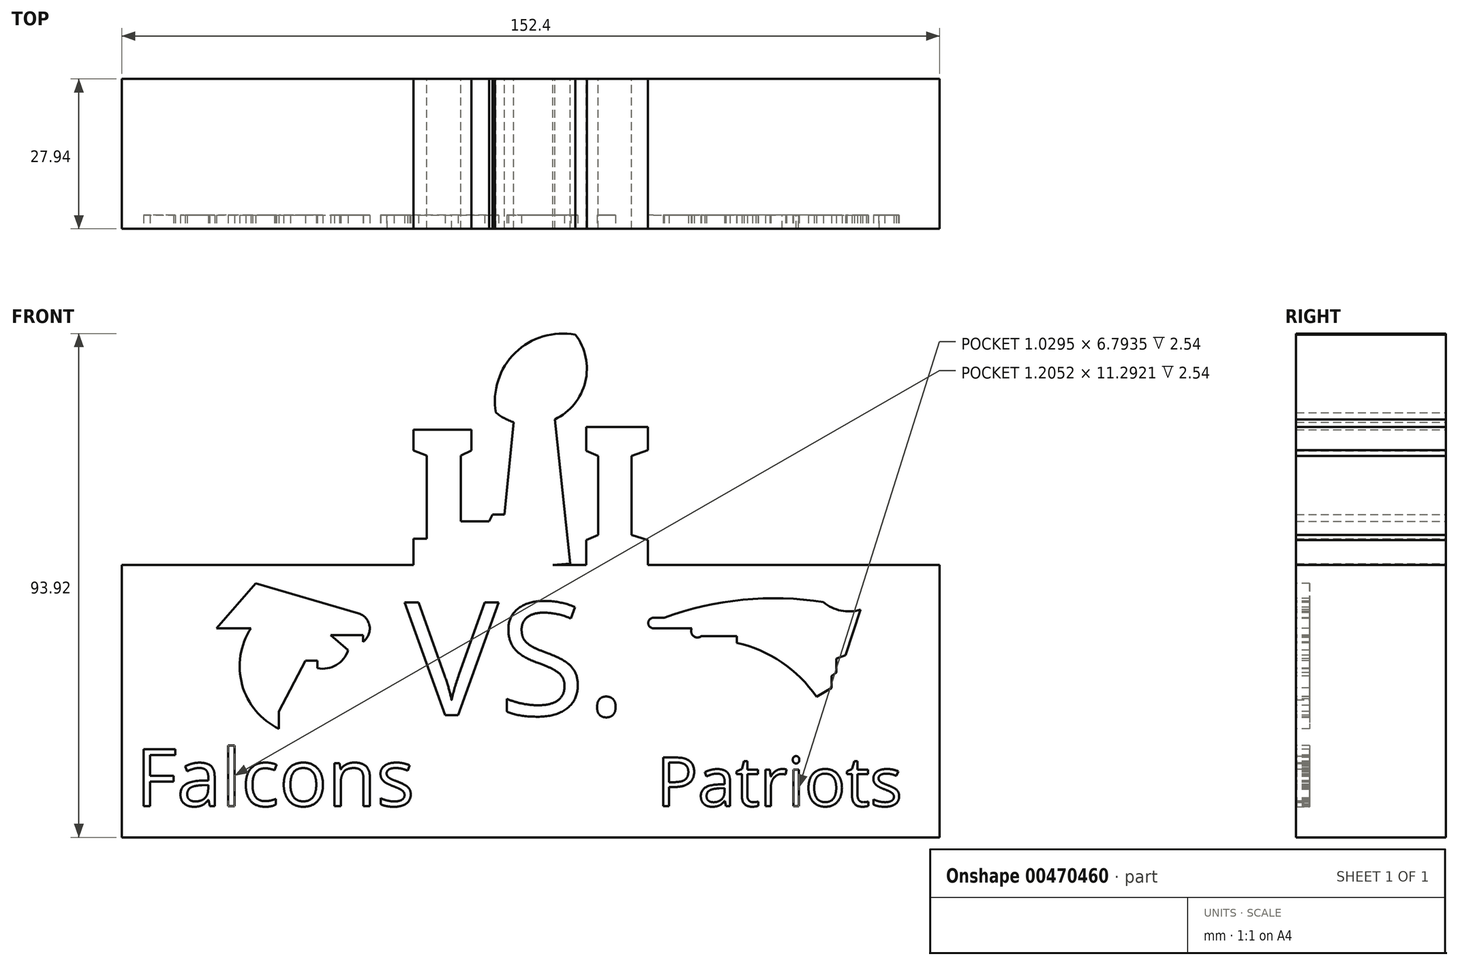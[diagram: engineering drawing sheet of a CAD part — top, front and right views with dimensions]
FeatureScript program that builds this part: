
annotation { "Feature Type Name" : "Feature", "Feature Type Description" : "" }
export const myFeature = defineFeature(function(context is Context, id is Id, definition is map)
    precondition{}
    {
        {
            var Q0;
            Q0=qCreatedBy(makeId("Front.planeOp"),FACE);
            var sketch = newSketch(context, id + "F0", { "sketchPlane" : qUnion([Q0])});
            skLineSegment(sketch, "E0.bottom", {"start": v(-75.1, 6.56) * mm, "end": v(77.3, 6.56) * mm});
            skLineSegment(sketch, "E0.top", {"start": v(-75.1, -44.24) * mm, "end": v(77.3, -44.24) * mm});
            skLineSegment(sketch, "E0.left", {"start": v(-75.1, 6.56) * mm, "end": v(-75.1, -44.24) * mm});
            skLineSegment(sketch, "E0.right", {"start": v(77.3, 6.56) * mm, "end": v(77.3, -44.24) * mm});
            skLineSegment(sketch, "E1", {"start": v(-20.74, 31.75) * mm, "end": v(-20.74, 27.9) * mm});
            skLineSegment(sketch, "E2", {"start": v(-20.74, 27.9) * mm, "end": v(-18.26, 26.95) * mm});
            skLineSegment(sketch, "E3", {"start": v(-18.26, 26.95) * mm, "end": v(-18.26, 11.44) * mm});
            skLineSegment(sketch, "E4", {"start": v(-18.26, 11.44) * mm, "end": v(-20.74, 11.44) * mm});
            skLineSegment(sketch, "E5", {"start": v(-20.74, 11.44) * mm, "end": v(-20.74, 6.56) * mm});
            skLineSegment(sketch, "E6", {"start": v(-20.74, 6.56) * mm, "end": v(5.21, 6.56) * mm});
            skLineSegment(sketch, "E7", {"start": v(3.63, 32.96) * mm, "end": v(5.21, 6.56) * mm});
            skLineSegment(sketch, "E8", {"start": v(5.21, 6.56) * mm, "end": v(8.44, 6.76) * mm});
            skLineSegment(sketch, "E9", {"start": v(8.44, 6.76) * mm, "end": v(5.6, 33.67) * mm});
            skLineSegment(sketch, "E10", {"start": v(-2.05, 33.14) * mm, "end": v(-3.76, 15.92) * mm});
            skLineSegment(sketch, "E11", {"start": v(-20.74, 31.75) * mm, "end": v(-9.95, 31.75) * mm});
            skLineSegment(sketch, "E12", {"start": v(-9.95, 31.75) * mm, "end": v(-9.95, 27.9) * mm});
            skLineSegment(sketch, "E13", {"start": v(-9.95, 27.9) * mm, "end": v(-11.92, 26.95) * mm});
            skLineSegment(sketch, "E14", {"start": v(-11.92, 26.95) * mm, "end": v(-11.92, 14.64) * mm});
            skLineSegment(sketch, "E15", {"start": v(-11.92, 14.64) * mm, "end": v(-6.63, 14.64) * mm});
            skLineSegment(sketch, "E16", {"start": v(-6.63, 14.64) * mm, "end": v(-6.03, 15.92) * mm});
            skLineSegment(sketch, "E17", {"start": v(-6.03, 15.92) * mm, "end": v(-3.76, 15.92) * mm});
            skLineSegment(sketch, "E18", {"start": v(-3.76, 15.92) * mm, "end": v(-3.76, 6.76) * mm});
            skArc(sketch, "E19", {"start": v(9.43, 49.45) * mm, "mid": v(-1.8, 46.07) * mm, "end": v(-5.4, 34.92) * mm});
            skArc(sketch, "E20", {"start": v(-5.4, 34.92) * mm, "mid": v(8.42, 35.64) * mm, "end": v(9.43, 49.45) * mm});
            skLineSegment(sketch, "E21", {"start": v(11.43, 27.82) * mm, "end": v(13.68, 26.87) * mm});
            skLineSegment(sketch, "E22", {"start": v(13.68, 26.87) * mm, "end": v(13.68, 12.13) * mm});
            skLineSegment(sketch, "E23", {"start": v(13.68, 12.13) * mm, "end": v(11.43, 11.19) * mm});
            skLineSegment(sketch, "E24", {"start": v(11.43, 11.19) * mm, "end": v(11.43, 6.56) * mm});
            skLineSegment(sketch, "E25", {"start": v(11.43, 6.56) * mm, "end": v(22.95, 6.56) * mm});
            skLineSegment(sketch, "E26", {"start": v(22.95, 6.56) * mm, "end": v(22.95, 11.19) * mm});
            skLineSegment(sketch, "E27", {"start": v(22.95, 11.19) * mm, "end": v(19.87, 12.13) * mm});
            skLineSegment(sketch, "E28", {"start": v(19.87, 12.13) * mm, "end": v(19.87, 26.87) * mm});
            skLineSegment(sketch, "E29", {"start": v(19.87, 26.87) * mm, "end": v(22.95, 27.95) * mm});
            skLineSegment(sketch, "E30", {"start": v(22.95, 27.95) * mm, "end": v(22.95, 32.23) * mm});
            skLineSegment(sketch, "E31", {"start": v(22.95, 32.23) * mm, "end": v(11.43, 32.23) * mm});
            skLineSegment(sketch, "E32", {"start": v(11.43, 32.23) * mm, "end": v(11.43, 27.82) * mm});
            skSolve(sketch);
        }
        {
            var Q0;
            Q0 = qSketchRegion(id + "F0", true);
            extrude(context, id + "F1", {"entities" : qUnion([Q0]), "depth" : 27.94 * mm});
        }
        {
            var Q0;
            Q0=makeQuery(id+"F1.opExtrude","CAP_FACE",FACE,{"disambiguationData":[OSD([sQuery(id+"F0.wireOp",EDGE,"E0.bottom"),sQuery(id+"F0.wireOp",EDGE,"E0.top"),sQuery(id+"F0.wireOp",EDGE,"E0.left"),sQuery(id+"F0.wireOp",EDGE,"E0.right"),sQuery(id+"F0.wireOp",EDGE,"51d3c1c2-4678-4070-a935-1c2ae8ceac52"),sQuery(id+"F0.wireOp",EDGE,"f5bbca2f-ece1-45e4-84c9-4250c47298a3"),sQuery(id+"F0.wireOp",EDGE,"df2c12da-2ae3-4d1a-bf00-16d2e73c16a6"),sQuery(id+"F0.wireOp",EDGE,"ab1d8fd3-a22a-4d10-bc1b-4df98c300e8c"),sQuery(id+"F0.wireOp",EDGE,"32629ec4-7446-44ef-b423-ef05bb4e758c"),sQuery(id+"F0.wireOp",EDGE,"b3cf064b-aa9a-4bf5-8094-2338da96f838"),sQuery(id+"F0.wireOp",EDGE,"5fee9cea-6940-4a30-ae6c-49024f08f099"),sQuery(id+"F0.wireOp",EDGE,"3d6fc4a5-3aed-420e-b1e3-99403f750af0"),sQuery(id+"F0.wireOp",EDGE,"caa3e821-e804-49dc-9bb2-aabf213cfac6"),sQuery(id+"F0.wireOp",EDGE,"841424ae-1137-4768-b8eb-4dc3a59ec455"),sQuery(id+"F0.wireOp",EDGE,"84873b07-a760-4daf-8af0-85f94e43fe12"),sQuery(id+"F0.wireOp",EDGE,"49e816f2-52c8-406e-a4e7-44763c2afad2"),sQuery(id+"F0.wireOp",EDGE,"f34c5290-1b6a-42fb-a69f-c831adc31d09"),sQuery(id+"F0.wireOp",EDGE,"a4cf80c3-0732-48e7-8c47-b4bcee52f594"),sQuery(id+"F0.wireOp",EDGE,"aa5594db-ee71-498d-9179-3ce95b60c7d9"),sQuery(id+"F0.wireOp",EDGE,"7350933a-e141-4493-ad32-cfc7d2644b59"),sQuery(id+"F0.wireOp",EDGE,"028e278e-2f42-4de1-bc6f-db93ac8ad055"),sQuery(id+"F0.wireOp",EDGE,"cfd26f7e-d5b0-4229-bcee-958b32301bc1"),sQuery(id+"F0.wireOp",EDGE,"caddbf1c-78cf-4739-9aeb-5831cae17361"),sQuery(id+"F0.wireOp",EDGE,"15cb3bb8-4a25-48d3-b514-d85eaaf90072"),sQuery(id+"F0.wireOp",EDGE,"1946ed44-b253-4600-8266-74096e4aaf0f"),sQuery(id+"F0.wireOp",EDGE,"8db78c25-9355-4392-b348-b02de26508c2"),sQuery(id+"F0.wireOp",EDGE,"97191c49-12d8-4a6f-9165-80d11d1dd639"),sQuery(id+"F0.wireOp",EDGE,"61e6cfa5-2e70-4e35-bf5d-c662ff1ec202"),sQuery(id+"F0.wireOp",EDGE,"a59ac232-1a09-4b81-823e-92916a3a9cf0"),sQuery(id+"F0.wireOp",EDGE,"431d7071-b944-4f6a-b879-15e466296cc0"),sQuery(id+"F0.wireOp",EDGE,"83490649-d1fb-4782-b3b2-dd4396876af3"),sQuery(id+"F0.wireOp",EDGE,"fea7df3c-3f4f-4230-b99d-b53fc99c95d4"),sQuery(id+"F0.wireOp",EDGE,"E1"),sQuery(id+"F0.wireOp",EDGE,"E2"),sQuery(id+"F0.wireOp",EDGE,"E3"),sQuery(id+"F0.wireOp",EDGE,"E4"),sQuery(id+"F0.wireOp",EDGE,"E5"),sQuery(id+"F0.wireOp",EDGE,"E8"),sQuery(id+"F0.wireOp",EDGE,"E9"),sQuery(id+"F0.wireOp",EDGE,"E10"),sQuery(id+"F0.wireOp",EDGE,"E11"),sQuery(id+"F0.wireOp",EDGE,"E12"),sQuery(id+"F0.wireOp",EDGE,"E13"),sQuery(id+"F0.wireOp",EDGE,"E14"),sQuery(id+"F0.wireOp",EDGE,"E15"),sQuery(id+"F0.wireOp",EDGE,"E16"),sQuery(id+"F0.wireOp",EDGE,"E17"),sQuery(id+"F0.wireOp",EDGE,"E19"),sQuery(id+"F0.wireOp",EDGE,"E20"),sQuery(id+"F0.wireOp",EDGE,"4a3dc4b8-d459-4231-ad36-f0e95a9c4572.sketch_text.stroke-0"),sQuery(id+"F0.wireOp",EDGE,"4a3dc4b8-d459-4231-ad36-f0e95a9c4572.sketch_text.stroke-1"),sQuery(id+"F0.wireOp",EDGE,"4a3dc4b8-d459-4231-ad36-f0e95a9c4572.sketch_text.stroke-2"),sQuery(id+"F0.wireOp",EDGE,"4a3dc4b8-d459-4231-ad36-f0e95a9c4572.sketch_text.stroke-3"),sQuery(id+"F0.wireOp",EDGE,"4a3dc4b8-d459-4231-ad36-f0e95a9c4572.sketch_text.stroke-4"),sQuery(id+"F0.wireOp",EDGE,"4a3dc4b8-d459-4231-ad36-f0e95a9c4572.sketch_text.stroke-5"),sQuery(id+"F0.wireOp",EDGE,"4a3dc4b8-d459-4231-ad36-f0e95a9c4572.sketch_text.stroke-6"),sQuery(id+"F0.wireOp",EDGE,"4a3dc4b8-d459-4231-ad36-f0e95a9c4572.sketch_text.stroke-7"),sQuery(id+"F0.wireOp",EDGE,"4a3dc4b8-d459-4231-ad36-f0e95a9c4572.sketch_text.stroke-8"),sQuery(id+"F0.wireOp",EDGE,"4a3dc4b8-d459-4231-ad36-f0e95a9c4572.sketch_text.stroke-9"),sQuery(id+"F0.wireOp",EDGE,"4a3dc4b8-d459-4231-ad36-f0e95a9c4572.sketch_text.stroke-10"),sQuery(id+"F0.wireOp",EDGE,"4a3dc4b8-d459-4231-ad36-f0e95a9c4572.sketch_text.stroke-11"),sQuery(id+"F0.wireOp",EDGE,"4a3dc4b8-d459-4231-ad36-f0e95a9c4572.sketch_text.stroke-12"),sQuery(id+"F0.wireOp",EDGE,"4a3dc4b8-d459-4231-ad36-f0e95a9c4572.sketch_text.stroke-13"),sQuery(id+"F0.wireOp",EDGE,"4a3dc4b8-d459-4231-ad36-f0e95a9c4572.sketch_text.stroke-14"),sQuery(id+"F0.wireOp",EDGE,"4a3dc4b8-d459-4231-ad36-f0e95a9c4572.sketch_text.stroke-15"),sQuery(id+"F0.wireOp",EDGE,"4a3dc4b8-d459-4231-ad36-f0e95a9c4572.sketch_text.stroke-16"),sQuery(id+"F0.wireOp",EDGE,"4a3dc4b8-d459-4231-ad36-f0e95a9c4572.sketch_text.stroke-17"),sQuery(id+"F0.wireOp",EDGE,"4a3dc4b8-d459-4231-ad36-f0e95a9c4572.sketch_text.stroke-18"),sQuery(id+"F0.wireOp",EDGE,"4a3dc4b8-d459-4231-ad36-f0e95a9c4572.sketch_text.stroke-19"),sQuery(id+"F0.wireOp",EDGE,"4a3dc4b8-d459-4231-ad36-f0e95a9c4572.sketch_text.stroke-20"),sQuery(id+"F0.wireOp",EDGE,"4a3dc4b8-d459-4231-ad36-f0e95a9c4572.sketch_text.stroke-21"),sQuery(id+"F0.wireOp",EDGE,"4a3dc4b8-d459-4231-ad36-f0e95a9c4572.sketch_text.stroke-22"),sQuery(id+"F0.wireOp",EDGE,"4a3dc4b8-d459-4231-ad36-f0e95a9c4572.sketch_text.stroke-23"),sQuery(id+"F0.wireOp",EDGE,"4a3dc4b8-d459-4231-ad36-f0e95a9c4572.sketch_text.stroke-24"),sQuery(id+"F0.wireOp",EDGE,"4a3dc4b8-d459-4231-ad36-f0e95a9c4572.sketch_text.stroke-25"),sQuery(id+"F0.wireOp",EDGE,"4a3dc4b8-d459-4231-ad36-f0e95a9c4572.sketch_text.stroke-26"),sQuery(id+"F0.wireOp",EDGE,"4a3dc4b8-d459-4231-ad36-f0e95a9c4572.sketch_text.stroke-27"),sQuery(id+"F0.wireOp",EDGE,"4a3dc4b8-d459-4231-ad36-f0e95a9c4572.sketch_text.stroke-28"),sQuery(id+"F0.wireOp",EDGE,"4a3dc4b8-d459-4231-ad36-f0e95a9c4572.sketch_text.stroke-29"),sQuery(id+"F0.wireOp",EDGE,"4a3dc4b8-d459-4231-ad36-f0e95a9c4572.sketch_text.stroke-30"),sQuery(id+"F0.wireOp",EDGE,"4a3dc4b8-d459-4231-ad36-f0e95a9c4572.sketch_text.stroke-31"),sQuery(id+"F0.wireOp",EDGE,"4a3dc4b8-d459-4231-ad36-f0e95a9c4572.sketch_text.stroke-32"),sQuery(id+"F0.wireOp",EDGE,"4a3dc4b8-d459-4231-ad36-f0e95a9c4572.sketch_text.stroke-33"),sQuery(id+"F0.wireOp",EDGE,"4a3dc4b8-d459-4231-ad36-f0e95a9c4572.sketch_text.stroke-34"),sQuery(id+"F0.wireOp",EDGE,"4a3dc4b8-d459-4231-ad36-f0e95a9c4572.sketch_text.stroke-35"),sQuery(id+"F0.wireOp",EDGE,"4a3dc4b8-d459-4231-ad36-f0e95a9c4572.sketch_text.stroke-36"),sQuery(id+"F0.wireOp",EDGE,"4a3dc4b8-d459-4231-ad36-f0e95a9c4572.sketch_text.stroke-37"),sQuery(id+"F0.wireOp",EDGE,"4a3dc4b8-d459-4231-ad36-f0e95a9c4572.sketch_text.stroke-38"),sQuery(id+"F0.wireOp",EDGE,"4a3dc4b8-d459-4231-ad36-f0e95a9c4572.sketch_text.stroke-39"),sQuery(id+"F0.wireOp",EDGE,"4a3dc4b8-d459-4231-ad36-f0e95a9c4572.sketch_text.stroke-40"),sQuery(id+"F0.wireOp",EDGE,"4a3dc4b8-d459-4231-ad36-f0e95a9c4572.sketch_text.stroke-41")])],"isStart":false});
            var sketch = newSketch(context, id + "F2", { "sketchPlane" : qUnion([Q0])});
            skText(sketch, "E33", { "text": "Falcons", "fontName": "OpenSans-Regular.ttf"});
            skText(sketch, "E34", { "text": "Patriots", "fontName": "OpenSans-Regular.ttf"});
            skArc(sketch, "E35", {"start": v(-51.04, -5.28) * mm, "mid": v(-52.67, -15.82) * mm, "end": v(-45.84, -24.01) * mm});
            skLineSegment(sketch, "E36", {"start": v(-51.04, -5.28) * mm, "end": v(-57.43, -5.28) * mm});
            skLineSegment(sketch, "E37", {"start": v(-57.43, -5.28) * mm, "end": v(-50.15, 3.11) * mm});
            skLineSegment(sketch, "E38", {"start": v(-50.15, 3.11) * mm, "end": v(-31.06, -2.46) * mm});
            skArc(sketch, "E39", {"start": v(-30.16, -7.81) * mm, "mid": v(-28.93, -4.86) * mm, "end": v(-31.06, -2.46) * mm});
            skLineSegment(sketch, "E40", {"start": v(-30.16, -7.81) * mm, "end": v(-30.16, -6.55) * mm});
            skLineSegment(sketch, "E41", {"start": v(-30.16, -6.55) * mm, "end": v(-36.18, -6.55) * mm});
            skLineSegment(sketch, "E42", {"start": v(-36.18, -6.55) * mm, "end": v(-32.93, -9.37) * mm});
            skArc(sketch, "E43", {"start": v(-38.63, -12.71) * mm, "mid": v(-35.15, -12.12) * mm, "end": v(-32.93, -9.37) * mm});
            skLineSegment(sketch, "E44", {"start": v(-38.63, -12.71) * mm, "end": v(-38.63, -11.3) * mm});
            skLineSegment(sketch, "E45", {"start": v(-38.63, -11.3) * mm, "end": v(-40.86, -11.3) * mm});
            skLineSegment(sketch, "E46", {"start": v(-40.86, -11.3) * mm, "end": v(-45.84, -20.74) * mm});
            skLineSegment(sketch, "E47", {"start": v(-45.84, -20.74) * mm, "end": v(-45.84, -24.01) * mm});
            skLineSegment(sketch, "E48", {"start": v(23.97, -3.32) * mm, "end": v(26, -3.32) * mm});
            skArc(sketch, "E49", {"start": v(23.97, -3.32) * mm, "mid": v(23, -4.3) * mm, "end": v(23.97, -5.27) * mm});
            skArc(sketch, "E50", {"start": v(55.67, -0.4) * mm, "mid": v(40.64, 0.03) * mm, "end": v(26, -3.32) * mm});
            skArc(sketch, "E51", {"start": v(55.67, -0.4) * mm, "mid": v(58.93, -1.99) * mm, "end": v(62.55, -1.78) * mm});
            skArc(sketch, "E52", {"start": v(54.34, -18) * mm, "mid": v(47.87, -11.62) * mm, "end": v(39.54, -7.98) * mm});
            skLineSegment(sketch, "E53", {"start": v(23.97, -5.27) * mm, "end": v(31.1, -5.27) * mm});
            skArc(sketch, "E54", {"start": v(31.1, -5.27) * mm, "mid": v(31.42, -6.7) * mm, "end": v(32.88, -6.75) * mm});
            skLineSegment(sketch, "E55", {"start": v(32.88, -6.75) * mm, "end": v(39.54, -6.75) * mm});
            skLineSegment(sketch, "E56", {"start": v(39.54, -6.75) * mm, "end": v(39.54, -7.98) * mm});
            skLineSegment(sketch, "E57", {"start": v(54.34, -18) * mm, "end": v(57.2, -16.38) * mm});
            skLineSegment(sketch, "E58", {"start": v(57.2, -16.38) * mm, "end": v(57.2, -14.18) * mm});
            skLineSegment(sketch, "E59", {"start": v(57.2, -14.18) * mm, "end": v(58.03, -13.52) * mm});
            skLineSegment(sketch, "E60", {"start": v(58.03, -13.52) * mm, "end": v(58.03, -10.95) * mm});
            skLineSegment(sketch, "E61", {"start": v(58.03, -10.95) * mm, "end": v(59.76, -10.3) * mm});
            skLineSegment(sketch, "E62", {"start": v(62.55, -1.78) * mm, "end": v(59.76, -10.3) * mm});
            skText(sketch, "E63", { "text": "VS.", "fontName": "OpenSans-Regular.ttf"});
            const initialGuessF2  = {"E33": [-0.07253, -0.0384, 1, 0, 0.0107], "E34": [0.02457, -0.03842, 1, 0, 0.00914], "E63": [-0.02237, -0.02147, 1, 0, 0.02118]};
            skSetInitialGuess(sketch, initialGuessF2);
            skSolve(sketch);
        }
        {
            var Q0;
            Q0 = qSketchRegion(id + "F2", true);
            extrude(context, id + "F3", {"entities" : qUnion([Q0]), "operationType" : NewBodyOperationType.REMOVE, "oppositeDirection" : true, "depth" : 2.54 * mm});
        }
    });
